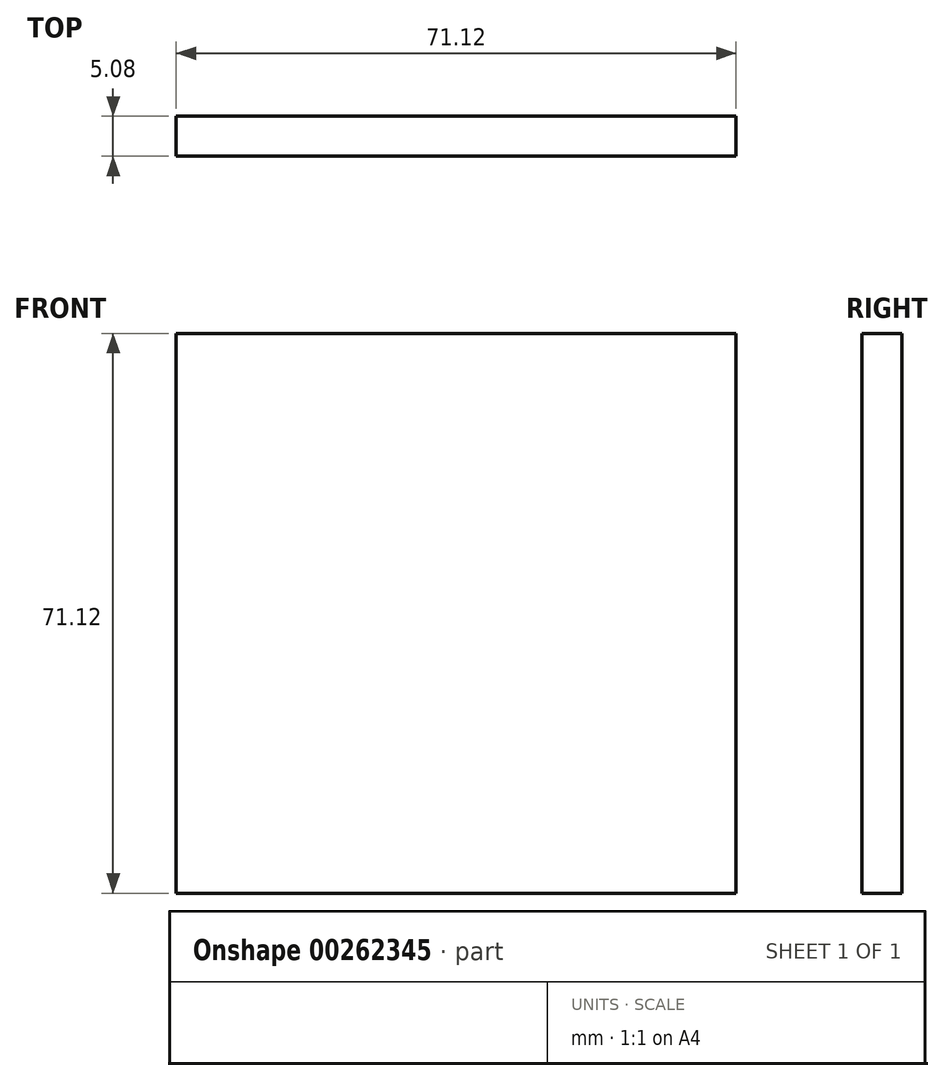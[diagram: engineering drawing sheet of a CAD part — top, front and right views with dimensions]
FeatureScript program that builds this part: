
annotation { "Feature Type Name" : "Feature", "Feature Type Description" : "" }
export const myFeature = defineFeature(function(context is Context, id is Id, definition is map)
    precondition{}
    {
        {
            var Q0;
            Q0=qCreatedBy(makeId("Front.planeOp"),FACE);
            var sketch = newSketch(context, id + "F0", { "sketchPlane" : qUnion([Q0])});
            skLineSegment(sketch, "E0.bottom", {"start": v(-35.56, 35.56) * mm, "end": v(35.56, 35.56) * mm});
            skLineSegment(sketch, "E0.top", {"start": v(-35.56, -35.56) * mm, "end": v(35.56, -35.56) * mm});
            skLineSegment(sketch, "E0.left", {"start": v(-35.56, 35.56) * mm, "end": v(-35.56, -35.56) * mm});
            skLineSegment(sketch, "E0.right", {"start": v(35.56, 35.56) * mm, "end": v(35.56, -35.56) * mm});
            skPoint(sketch, "E0.middle", {"position": v(0, 0) * mm});
            skSolve(sketch);
        }
        {
            var Q0;
            Q0 = qSketchRegion(id + "F0", true);
            extrude(context, id + "F1", {"entities" : qUnion([Q0]), "depth" : 5.08 * mm});
        }
    });
